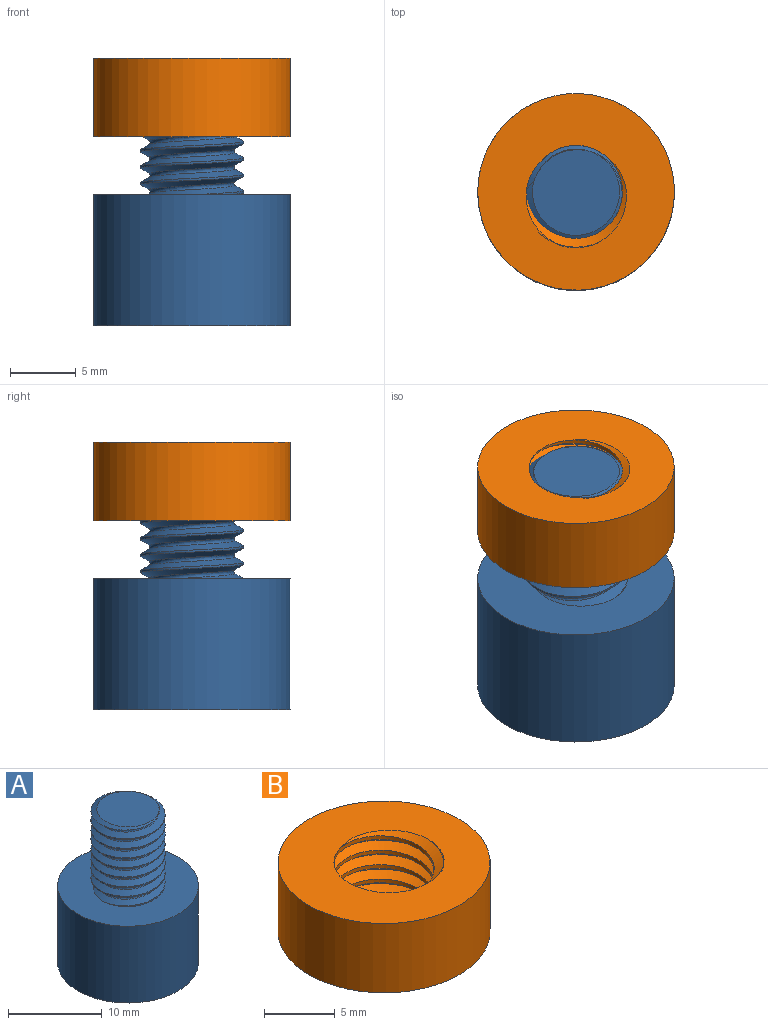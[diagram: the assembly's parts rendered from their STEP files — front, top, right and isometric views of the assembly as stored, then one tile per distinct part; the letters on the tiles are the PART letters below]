
ASSEMBLY  parts=2 mates=1
PART A: 9 faces, bbox 15.3x15.3x20.8 mm
  f0: cylinder r=3.94mm len=9.69mm, axis (0,0,-1), area 15.8mm2, adj f3,f4,f5,f8
  f1: plane 6.68x6.58mm, normal (0,0,1), area 34.1mm2, adj f2,f3,f4,f5
  f2: bspline ~10.94x7.55mm, area 56.7mm2, adj f1,f3,f4,f8
  f3: bspline ~11.02x9.11mm, area 139.8mm2, adj f0,f1,f2,f5,f8
  f4: bspline ~10.6x9.11mm, area 139.9mm2, adj f0,f1,f2,f5,f8
  f5: cone r=3.94mm half-angle=63.4deg, axis (0,0,-1), area 6.5mm2, adj f0,f1,f3,f4
  f6: plane 15x15mm, normal (0,0,-1), area 176.7mm2, adj f7
  f7: cylinder r=7.5mm len=15mm, axis (0,0,1), area 471.2mm2, adj f6,f8
  f8: plane 15.35x15.35mm, normal (0,0,1), area 136.8mm2, adj f0,f2,f3,f4,f7
PART B: 7 faces, bbox 15.4x15.4x7.4 mm
  f0: cylinder r=7.5mm len=15mm, axis (0,0,-1), area 282.7mm2, adj f1,f2
  f1: plane 15.34x15.34mm, normal (0,0,1), area 130.1mm2, adj f0,f3,f4,f5,f6
  f2: plane 15.37x15.37mm, normal (0,0,-1), area 130.1mm2, adj f0,f3,f4,f5,f6
  f3: bspline ~9.75x8.44mm, area 91.5mm2, adj f1,f2,f5,f6
  f4: bspline ~9.75x8.44mm, area 91.7mm2, adj f1,f2,f5,f6
  f5: bspline ~9.88x8.56mm, area 23.2mm2, adj f1,f2,f3,f4
  f6: cylinder r=3.54mm len=7.09mm, axis (0,0,1), area 33.3mm2, adj f1,f2,f3,f4
PLACE A rot(axis=(0,0,1),90deg) t=(-4.5,64.5,0)mm
PLACE B rot(axis=(0,0,-1),60deg) t=(-35.65,-22.87,4.42)mm
MATE cylindrical B.f0 <-> A.f0  axis (0,0,1) through (-34.5,30,10.42)mm
